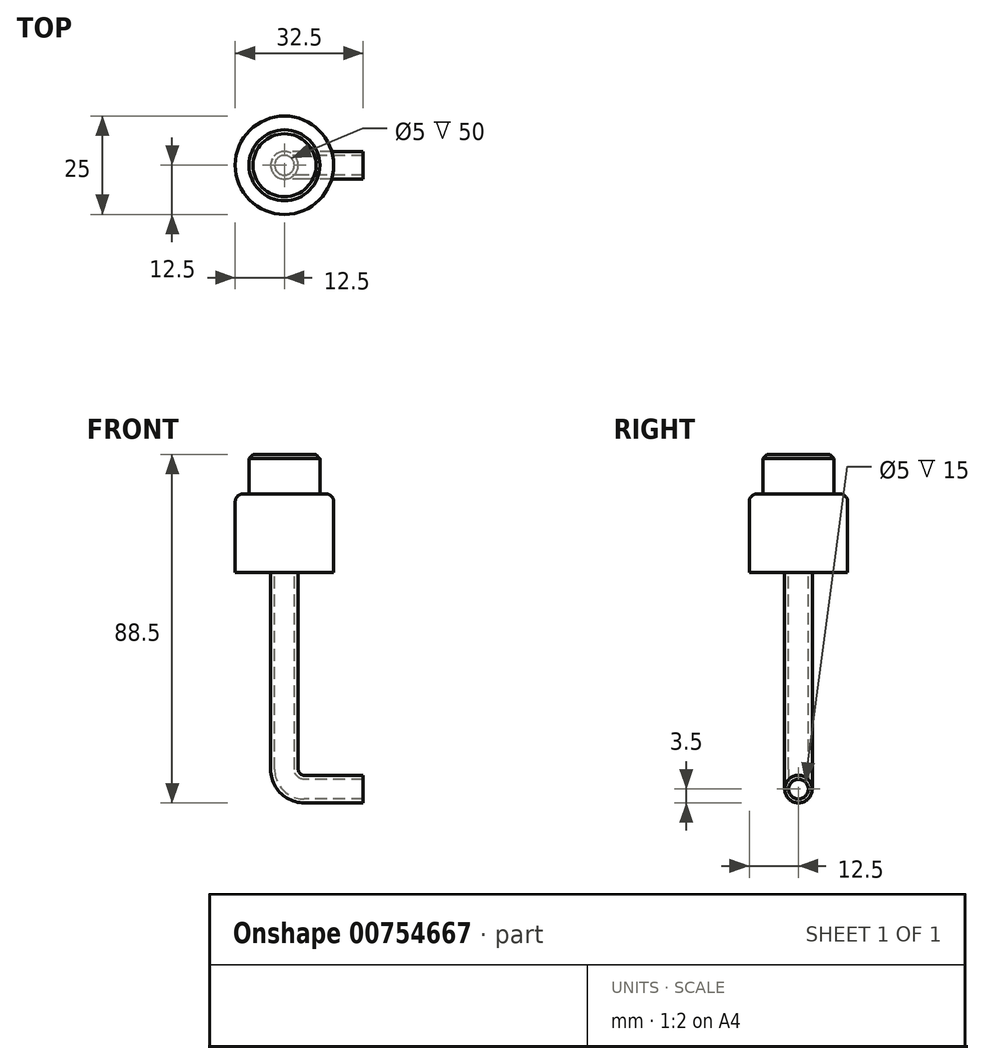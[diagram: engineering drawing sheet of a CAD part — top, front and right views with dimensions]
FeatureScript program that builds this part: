
annotation { "Feature Type Name" : "Feature", "Feature Type Description" : "" }
export const myFeature = defineFeature(function(context is Context, id is Id, definition is map)
    precondition{}
    {
        {
            var Q0;
            Q0=qCreatedBy(makeId("Top.planeOp"),FACE);
            var sketch = newSketch(context, id + "F0", { "sketchPlane" : qUnion([Q0])});
            skCircle(sketch, "E0", {"center": v(0, 0) * mm, "radius": 12.5 * mm});
            skSolve(sketch);
        }
        {
            var Q0;
            Q0=makeQuery(id+"F0.imprint","IMPRINT",FACE,{"disambiguationData":[TD([[makeQuery(id+"F0.imprint","IMPRINT",EDGE,{"derivedFrom":sQuery(id+"F0.wireOp",EDGE,"E0")}),1.0]])]});
            extrude(context, id + "F1", {"entities" : qUnion([Q0]), "depth" : 20 * mm, "offsetDistance" : 25 * mm});
        }
        {
            var Q0;
            Q0=makeQuery(id+"F1.opExtrude","CAP_FACE",FACE,{"disambiguationData":[OSD([sQuery(id+"F0.wireOp",EDGE,"E0")])],"isStart":false});
            var sketch = newSketch(context, id + "F2", { "sketchPlane" : qUnion([Q0])});
            skCircle(sketch, "E1", {"center": v(0, 0) * mm, "radius": 9 * mm});
            skSolve(sketch);
        }
        {
            var Q0;
            Q0=makeQuery(id+"F2.imprint","IMPRINT",FACE,{"disambiguationData":[TD([[makeQuery(id+"F2.imprint","IMPRINT",EDGE,{"derivedFrom":sQuery(id+"F2.wireOp",EDGE,"E1")}),1.0]])]});
            extrude(context, id + "F3", {"entities" : qUnion([Q0]), "operationType" : NewBodyOperationType.ADD, "depth" : 10 * mm, "offsetDistance" : 25 * mm});
        }
        {
            var Q0;
            Q0=makeQuery(id+"F3.opExtrude","CAP_FACE",FACE,{"disambiguationData":[OSD([sQuery(id+"F2.wireOp",EDGE,"E1")])],"isStart":false});
            var sketch = newSketch(context, id + "F4", { "sketchPlane" : qUnion([Q0])});
            skCircle(sketch, "E2", {"center": v(0, 0) * mm, "radius": 7.5 * mm});
            skSolve(sketch);
        }
        {
            var Q0;
            Q0=makeQuery(id+"F4.imprint","IMPRINT",FACE,{"disambiguationData":[TD([[makeQuery(id+"F4.imprint","IMPRINT",EDGE,{"derivedFrom":sQuery(id+"F4.wireOp",EDGE,"E2")}),1.0]])]});
            extrude(context, id + "F5", {"entities" : qUnion([Q0]), "operationType" : NewBodyOperationType.ADD, "depth" : 20 * mm, "offsetDistance" : 25 * mm});
        }
        {
            var Q0;
            Q0=makeQuery(id+"F1.opExtrude","CAP_EDGE",EDGE,{"disambiguationData":[OSD([sQuery(id+"F0.wireOp",EDGE,"E0")])],"isStart":false});
            fillet(context, id + "F6", {"entities" : qUnion([Q0]), "radius" : 2 * mm, "tangentPropagation" : true, "allowEdgeOverflow" : false});
        }
        {
            var Q0;
            Q0=makeQuery(id+"F3.opExtrude","CAP_EDGE",EDGE,{"disambiguationData":[OSD([sQuery(id+"F2.wireOp",EDGE,"E1")])],"isStart":false});
            chamfer(context, id + "F7", {"entities" : qUnion([Q0]), "width" : 1 * mm, "tangentPropagation" : true});
        }
        {
            var Q0;
            Q0=makeQuery(id+"F5.opExtrude","CAP_EDGE",EDGE,{"disambiguationData":[OSD([sQuery(id+"F4.wireOp",EDGE,"E2")])],"isStart":false});
            fillet(context, id + "F8", {"entities" : qUnion([Q0]), "radius" : 1 * mm, "tangentPropagation" : true, "allowEdgeOverflow" : false});
        }
        {
            var Q0;
            Q0=qCreatedBy(makeId("Front.planeOp"),FACE);
            var sketch = newSketch(context, id + "F9", { "sketchPlane" : qUnion([Q0])});
            skCircle(sketch, "E3", {"center": v(0, 45) * mm, "radius": 2.5 * mm});
            skCircle(sketch, "E4", {"center": v(0, 45) * mm, "radius": 2 * mm});
            skSolve(sketch);
        }
        {
            var Q0;
            Q0 = qSketchRegion(id + "F9", true);
            extrude(context, id + "F10", {"entities" : qUnion([Q0]), "operationType" : NewBodyOperationType.REMOVE, "depth" : 25 * mm, "offsetDistance" : 25 * mm});
        }
        {
            var Q0;
            Q0=makeQuery(id+"F1.opExtrude","CAP_FACE",FACE,{"disambiguationData":[OSD([sQuery(id+"F0.wireOp",EDGE,"E0")])],"isStart":true});
            var sketch = newSketch(context, id + "F11", { "sketchPlane" : qUnion([Q0])});
            skCircle(sketch, "E5", {"center": v(0, 0) * mm, "radius": 3.5 * mm});
            skCircle(sketch, "E6", {"center": v(0, 0) * mm, "radius": 2.5 * mm});
            skSolve(sketch);
        }
        {
            var Q0;
            Q0=makeQuery(id+"F11.imprint","IMPRINT",FACE,{"disambiguationData":[TD([[makeQuery(id+"F11.imprint","IMPRINT",EDGE,{"derivedFrom":sQuery(id+"F11.wireOp",EDGE,"E5")}),1.0]])]});
            extrude(context, id + "F12", {"entities" : qUnion([Q0]), "operationType" : NewBodyOperationType.ADD, "depth" : 50 * mm, "offsetDistance" : 25 * mm});
        }
        {
            var Q0;
            Q0=makeQuery(id+"F5.opExtrude","CAP_FACE",FACE,{"disambiguationData":[OSD([sQuery(id+"F4.wireOp",EDGE,"E2")])],"isStart":false});
            var sketch = newSketch(context, id + "F13", { "sketchPlane" : qUnion([Q0])});
            skCircle(sketch, "E7", {"center": v(0, 0) * mm, "radius": 26.64 * mm});
            skSolve(sketch);
        }
        {
            var Q0;
            Q0=makeQuery(id+"F13.imprint","IMPRINT",FACE,{"disambiguationData":[TD([[makeQuery(id+"F13.imprint","IMPRINT",EDGE,{"derivedFrom":sQuery(id+"F13.wireOp",EDGE,"E7")}),1.0]])]});
            var Q1;
            {var subQ0=sQuery(id+"F4.wireOp",EDGE,"E2");Q1=makeQuery(id+"F13.imprint","IMPRINT",FACE,{"disambiguationData":[TD([[makeQuery(id+"F13.imprint","IMPRINT",EDGE,{"derivedFrom":makeQuery(id+"F8.opFillet","BLEND_EDGE",EDGE,{"blendedFrom":[makeQuery(id+"F5.opExtrude","CAP_EDGE",EDGE,{"disambiguationData":[OSD([subQ0])],"isStart":false}),makeQuery(id+"F5.opExtrude","CAP_FACE",FACE,{"disambiguationData":[OSD([subQ0])],"isStart":false})],"blendedInto":[makeQuery(id+"F5.opExtrude","CAP_FACE",FACE,{"disambiguationData":[OSD([subQ0])],"isStart":false})]})}),1.0]])]});}
            var Q2;
            Q2=makeQuery(id+"F3.opExtrude","CAP_FACE",FACE,{"disambiguationData":[OSD([sQuery(id+"F2.wireOp",EDGE,"E1")])],"isStart":false});
            extrude(context, id + "F14", {"entities" : qUnion([Q0, Q1]), "operationType" : NewBodyOperationType.REMOVE, "endBound" : BoundingType.UP_TO_SURFACE, "oppositeDirection" : true, "depth" : 25 * mm, "endBoundEntityFace" : qUnion([Q2]), "offsetDistance" : 25 * mm});
        }
        {
            var Q0;
            Q0=qCreatedBy(makeId("Front.planeOp"),FACE);
            var sketch = newSketch(context, id + "F15", { "sketchPlane" : qUnion([Q0])});
            skArc(sketch, "E8", {"start": v(0, -50) * mm, "mid": v(1.46, -53.54) * mm, "end": v(5, -55) * mm});
            skSolve(sketch);
        }
        {
            var Q0;
            Q0=makeQuery(id+"F12.opExtrude","CAP_FACE",FACE,{"disambiguationData":[OSD([sQuery(id+"F11.wireOp",EDGE,"E5"),sQuery(id+"F11.wireOp",EDGE,"E6")])],"isStart":false});
            var Q1;
            Q1=sQuery(id+"F15.wireOp",EDGE,"E8");
            sweep(context, id + "F16", {"operationType" : NewBodyOperationType.ADD, "profiles" : qUnion([Q0]), "path" : qUnion([Q1])});
        }
        {
            var Q0;
            Q0=makeQuery(id+"F16.opSweep","CAP_FACE",FACE,{"disambiguationData":[OSD([sQuery(id+"F11.wireOp",EDGE,"E5"),sQuery(id+"F11.wireOp",EDGE,"E6"),sQuery(id+"F15.wireOp",VERTEX,"E8.end")])],"isStart":false});
            extrude(context, id + "F17", {"entities" : qUnion([Q0]), "operationType" : NewBodyOperationType.ADD, "depth" : 15 * mm, "offsetDistance" : 25 * mm});
        }
    });
